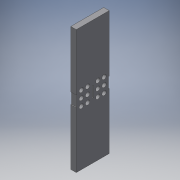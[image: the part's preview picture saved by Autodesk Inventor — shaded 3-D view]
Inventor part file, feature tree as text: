
AUTODESK INVENTOR PART (.ipt)
format: ipt  version: 2016 (Build 200138000, 138)  size: 301,056 bytes
history: native  units: in
note: dims shown in document units (in); Inventor stores cm internally (conversion verified against a paired STEP export)
features: reference x8, extrude x4, sketch x4, fillet x2, chamfer x1
ambient origin geometry x8: Origin, YZ Plane, XZ Plane, XY Plane, X Axis, Y Axis, Z Axis, Center Point
bodies: Solid1 (feature_tree)
feature tree (19):
  extrude  "Extrusion1"  Depth=1.1811in
  extrude  "Extrusion2"  Depth=0.3937in TaperAngle=0.0deg
  fillet  "Fillet1"  Radius=0.073in
  extrude  "Extrusion3"  Depth=0.0197in
  extrude  "Extrusion4"  Depth=0.0118in
  chamfer  "Chamfer1"  Distance=0.0787in
  fillet  "Fillet2"  Radius=0.7874in
  sketch  "Sketch1"  dims[d0=0.0748in d1=1.1811in d3=0.1in d4=0.7874in d6=0.0902in]
  sketch  "Sketch2"  dims[d9=0.7874in d11=0.2362in d12=0.3937in d14=1.0in d16=0.0787in d17=0.0in d18=0.073in]
  sketch  "Sketch3"  dims[d19=0.073in d20=0.0197in]
  reference  "Reference1"
  reference  "Reference2"
  reference  "Reference3"
  reference  "Reference4"
  sketch  "Sketch4"  dims[d21=0.1575in d22=0.7874in d24=0.2362in d25=0.7874in d27=0.2362in d30=0.0787in d31=0.0in d32=0.7874in d33=0.7874in d34=0.0118in d35=1.0in d36=0.0in d37=1.0in d38=0.0in d39=0.0197in d40=0.125in d41=45.0deg d42=0.0118in]
  reference  "Reference5"
  reference  "Reference6"
  reference  "Reference7"
  reference  "Reference8"
